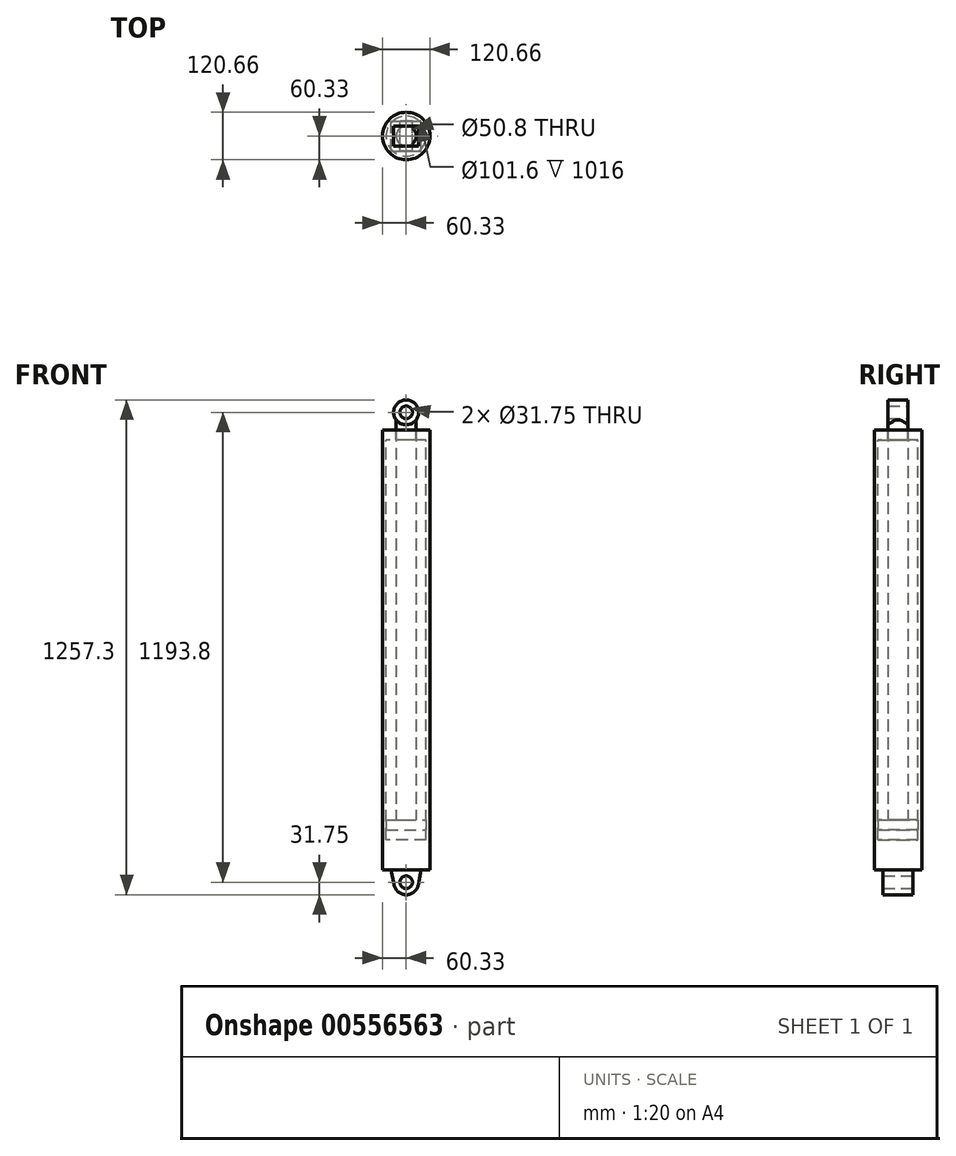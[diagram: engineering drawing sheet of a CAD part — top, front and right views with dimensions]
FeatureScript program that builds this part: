
annotation { "Feature Type Name" : "Feature", "Feature Type Description" : "" }
export const myFeature = defineFeature(function(context is Context, id is Id, definition is map)
    precondition{}
    {
        {
            var Q0;
            Q0=qCreatedBy(makeId("Front.planeOp"),FACE);
            var sketch = newSketch(context, id + "F0", { "sketchPlane" : qUnion([Q0])});
            skLineSegment(sketch, "E0.bottom", {"start": v(-60.32, 1117.6) * mm, "end": v(-25.4, 1117.6) * mm, "construction": true});
            skLineSegment(sketch, "E0.left", {"start": v(-60.33, 1117.6) * mm, "end": v(-60.33, 0) * mm, "construction": true});
            skLineSegment(sketch, "E0.right", {"start": v(60.32, 1117.6) * mm, "end": v(60.32, 0) * mm});
            skLineSegment(sketch, "E1.left", {"start": v(-50.8, 1092.2) * mm, "end": v(-50.8, 76.2) * mm, "construction": true});
            skLineSegment(sketch, "E1.right", {"start": v(50.8, 1092.2) * mm, "end": v(50.8, 76.2) * mm});
            skLineSegment(sketch, "E2", {"start": v(-25.4, 1117.6) * mm, "end": v(-25.4, 1092.2) * mm, "construction": true});
            skLineSegment(sketch, "E3", {"start": v(-25.4, 1092.2) * mm, "end": v(-50.8, 1092.2) * mm, "construction": true});
            skLineSegment(sketch, "E4", {"start": v(25.4, 1117.6) * mm, "end": v(25.4, 1092.2) * mm});
            skLineSegment(sketch, "E5", {"start": v(25.4, 1092.2) * mm, "end": v(50.8, 1092.2) * mm});
            skLineSegment(sketch, "E6.trimOffspring", {"start": v(25.4, 1117.6) * mm, "end": v(60.32, 1117.6) * mm});
            skLineSegment(sketch, "E7", {"start": v(0, 76.2) * mm, "end": v(0, 0) * mm});
            skLineSegment(sketch, "E8", {"start": v(0, 76.2) * mm, "end": v(50.8, 76.2) * mm});
            skLineSegment(sketch, "E9", {"start": v(0, 0) * mm, "end": v(60.32, 0) * mm});
            skLineSegment(sketch, "E10", {"start": v(-60.33, 0) * mm, "end": v(0, 0) * mm, "construction": true});
            skLineSegment(sketch, "E11", {"start": v(-50.8, 76.2) * mm, "end": v(0, 76.2) * mm, "construction": true});
            skSolve(sketch);
        }
        {
            var Q0;
            Q0 = qSketchRegion(id + "F0", true);
            var Q1;
            Q1=sQuery(id+"F0.wireOp",EDGE,"E7");
            revolve(context, id + "F1", {"entities" : qUnion([Q0]), "axis" : qUnion([Q1]), "revolveType" : RevolveType.FULL});
        }
        {
            var Q0;
            Q0=qCreatedBy(makeId("Front.planeOp"),FACE);
            var sketch = newSketch(context, id + "F2", { "sketchPlane" : qUnion([Q0])});
            skCircle(sketch, "E12", {"center": v(0, -31.75) * mm, "radius": 15.88 * mm});
            skArc(sketch, "E13", {"start": v(-31.23, -37.48) * mm, "mid": v(0, -63.5) * mm, "end": v(31.23, -37.48) * mm});
            skLineSegment(sketch, "E14", {"start": v(38.1, 0) * mm, "end": v(31.23, -37.48) * mm});
            skLineSegment(sketch, "E15", {"start": v(-38.1, 0) * mm, "end": v(-31.23, -37.48) * mm});
            skLineSegment(sketch, "E16", {"start": v(-38.1, 0) * mm, "end": v(38.1, 0) * mm});
            skSolve(sketch);
        }
        {
            var Q0;
            Q0 = qSketchRegion(id + "F2", true);
            extrude(context, id + "F3", {"entities" : qUnion([Q0]), "operationType" : NewBodyOperationType.ADD, "endBound" : BoundingType.SYMMETRIC, "depth" : 76.2 * mm, "offsetDistance" : 25.4 * mm});
        }
        {
            var Q0;
            Q0=qCreatedBy(makeId("Front.planeOp"),FACE);
            var sketch = newSketch(context, id + "F4", { "sketchPlane" : qUnion([Q0])});
            skLineSegment(sketch, "E17", {"start": v(-25.4, 1143) * mm, "end": v(-25.4, 127) * mm});
            skLineSegment(sketch, "E18", {"start": v(-25.4, 127) * mm, "end": v(-50.8, 127) * mm});
            skLineSegment(sketch, "E19", {"start": v(-50.8, 127) * mm, "end": v(-50.8, 101.6) * mm});
            skLineSegment(sketch, "E20", {"start": v(-50.8, 101.6) * mm, "end": v(0, 101.6) * mm});
            skLineSegment(sketch, "E21", {"start": v(0, 101.6) * mm, "end": v(0, 1143) * mm});
            skLineSegment(sketch, "E22", {"start": v(0, 1143) * mm, "end": v(-25.4, 1143) * mm});
            skSolve(sketch);
        }
        {
            var Q0;
            Q0 = qSketchRegion(id + "F4", true);
            var Q1;
            Q1=sQuery(id+"F4.wireOp",EDGE,"E21");
            revolve(context, id + "F5", {"entities" : qUnion([Q0]), "axis" : qUnion([Q1]), "revolveType" : RevolveType.FULL});
        }
        {
            var Q0;
            Q0=qCreatedBy(makeId("Front.planeOp"),FACE);
            var sketch = newSketch(context, id + "F6", { "sketchPlane" : qUnion([Q0])});
            skCircle(sketch, "E23", {"center": v(0, 1162.05) * mm, "radius": 15.88 * mm});
            skCircle(sketch, "E24", {"center": v(0, 1162.05) * mm, "radius": 31.75 * mm});
            skLineSegment(sketch, "E25", {"start": v(-25.4, 1143) * mm, "end": v(25.4, 1143) * mm, "construction": true});
            skSolve(sketch);
        }
        {
            var Q0;
            Q0 = qSketchRegion(id + "F6", true);
            extrude(context, id + "F7", {"entities" : qUnion([Q0]), "operationType" : NewBodyOperationType.ADD, "endBound" : BoundingType.SYMMETRIC, "depth" : 50.8 * mm, "offsetDistance" : 25.4 * mm});
        }
        {
            var Q0;
            Q0=makeQuery(id+"F1.opRevolve","SWEPT_BODY",BODY,{"disambiguationData":[OSD([sQuery(id+"F0.wireOp",EDGE,"E0.right"),sQuery(id+"F0.wireOp",EDGE,"E1.right"),sQuery(id+"F0.wireOp",EDGE,"E4"),sQuery(id+"F0.wireOp",EDGE,"E5"),sQuery(id+"F0.wireOp",EDGE,"E6.trimOffspring"),sQuery(id+"F0.wireOp",EDGE,"E7"),sQuery(id+"F0.wireOp",EDGE,"E8"),sQuery(id+"F0.wireOp",EDGE,"E9")])]});
            transform(context, id + "F8", {"entities" : qUnion([Q0]), "transformType" : TransformType.TRANSLATION_3D, "dx" : 0 * mm, "dy" : 0 * mm, "dz" : 0 * mm, "makeCopy" : true});
        }
        {
            var Q0;
            Q0=makeQuery(id+"F8.opPattern","COPY",BODY,{"derivedFrom":makeQuery(id+"F1.opRevolve","SWEPT_BODY",BODY,{"disambiguationData":[OSD([sQuery(id+"F0.wireOp",EDGE,"E0.right"),sQuery(id+"F0.wireOp",EDGE,"E1.right"),sQuery(id+"F0.wireOp",EDGE,"E4"),sQuery(id+"F0.wireOp",EDGE,"E5"),sQuery(id+"F0.wireOp",EDGE,"E6.trimOffspring"),sQuery(id+"F0.wireOp",EDGE,"E7"),sQuery(id+"F0.wireOp",EDGE,"E8"),sQuery(id+"F0.wireOp",EDGE,"E9")])]}),"instanceName":"1"});
            deleteBodies(context, id + "F9", {"entities" : qUnion([Q0])});
        }
    });
